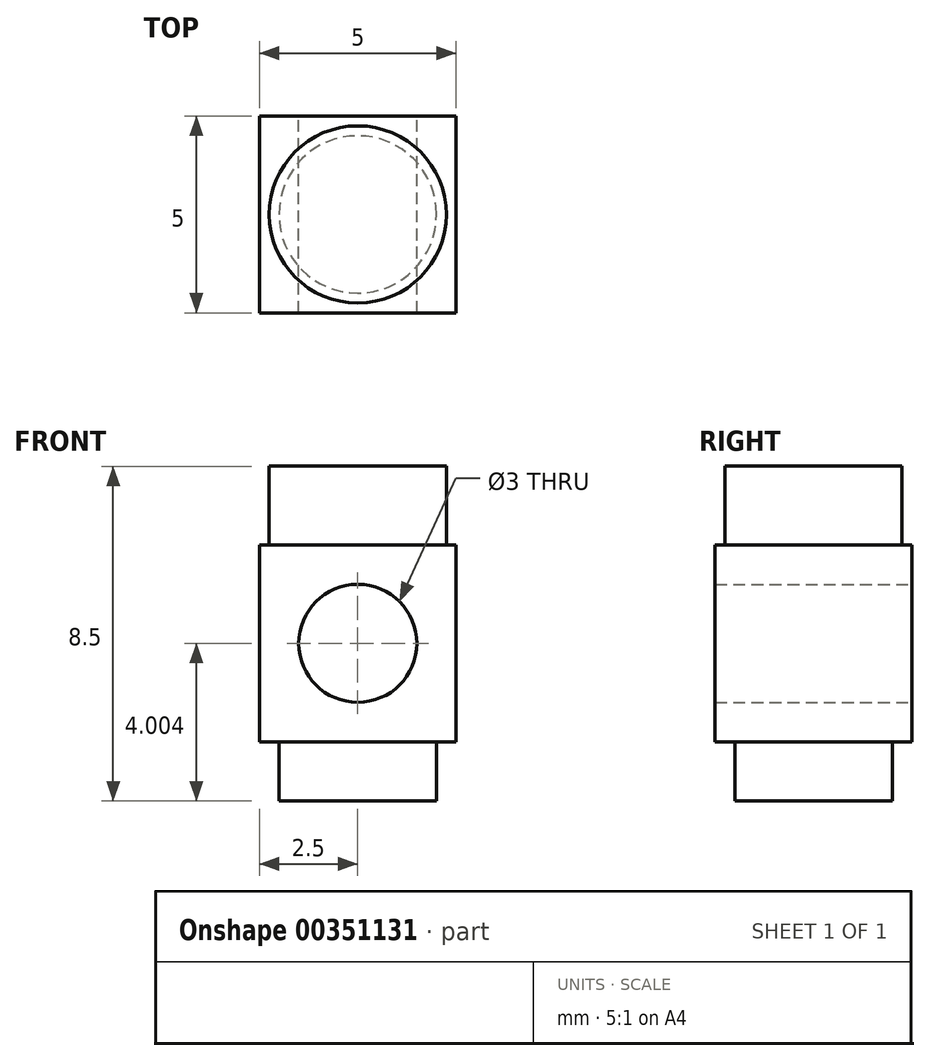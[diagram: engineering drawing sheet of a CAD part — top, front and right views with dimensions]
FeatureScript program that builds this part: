
annotation { "Feature Type Name" : "Feature", "Feature Type Description" : "" }
export const myFeature = defineFeature(function(context is Context, id is Id, definition is map)
    precondition{}
    {
        {
            var Q0;
            Q0=qCreatedBy(makeId("Front.planeOp"),FACE);
            var sketch = newSketch(context, id + "F0", { "sketchPlane" : qUnion([Q0])});
            skLineSegment(sketch, "E0.bottom", {"start": v(0, 12.57) * mm, "end": v(5, 12.57) * mm});
            skLineSegment(sketch, "E0.top", {"start": v(0, 17.57) * mm, "end": v(5, 17.57) * mm});
            skLineSegment(sketch, "E0.left", {"start": v(0, 12.57) * mm, "end": v(0, 17.57) * mm});
            skLineSegment(sketch, "E0.right", {"start": v(5, 12.57) * mm, "end": v(5, 17.57) * mm});
            skLineSegment(sketch, "E1", {"start": v(0, 17.57) * mm, "end": v(2.5, 17.57) * mm, "construction": true});
            skLineSegment(sketch, "E2", {"start": v(2.5, 17.57) * mm, "end": v(2.5, 12.57) * mm, "construction": true});
            skLineSegment(sketch, "E3", {"start": v(2.5, 12.57) * mm, "end": v(0, 12.57) * mm, "construction": true});
            skLineSegment(sketch, "E4", {"start": v(0, 15.07) * mm, "end": v(5, 15.07) * mm, "construction": true});
            skPoint(sketch, "E5", {"position": v(2.5, 15.07) * mm});
            skSolve(sketch);
        }
        {
            var Q0;
            Q0=makeQuery(id+"F0.imprint","IMPRINT",FACE,{"disambiguationData":[TD([[makeQuery(id+"F0.imprint","IMPRINT",EDGE,{"derivedFrom":sQuery(id+"F0.wireOp",EDGE,"E0.bottom")}),1.0]])]});
            extrude(context, id + "F1", {"entities" : qUnion([Q0]), "depth" : 5 * mm});
        }
        {
            var Q0;
            Q0=sQuery(id+"F0.wireOp",VERTEX,"E5");
            var Q1;
            Q1=makeQuery(id+"F1.opExtrude","SWEPT_BODY",BODY,{"disambiguationData":[OSD([sQuery(id+"F0.wireOp",EDGE,"E0.bottom"),sQuery(id+"F0.wireOp",EDGE,"E0.top"),sQuery(id+"F0.wireOp",EDGE,"E0.left"),sQuery(id+"F0.wireOp",EDGE,"E0.right")])]});
            hole(context, id + "F2", {"style" : HoleStyle.SIMPLE, "endStyle" : HoleEndStyle.THROUGH, "oppositeDirection" : true, "holeDiameter" : 3 * mm, "isTappedThrough" : true, "tappedDepth" : 12 * mm, "tapClearance" : 3, "locations" : qUnion([Q0]), "scope" : qUnion([Q1])});
        }
        {
            var Q0;
            Q0=makeQuery(id+"F1.opExtrude","SWEPT_FACE",FACE,{"disambiguationData":[OSD([sQuery(id+"F0.wireOp",EDGE,"E0.top")])]});
            var sketch = newSketch(context, id + "F3", { "sketchPlane" : qUnion([Q0])});
            skLineSegment(sketch, "E6", {"start": v(2.5, 0) * mm, "end": v(2.5, -5) * mm, "construction": true});
            skLineSegment(sketch, "E7", {"start": v(2.5, -5) * mm, "end": v(5, -5) * mm, "construction": true});
            skLineSegment(sketch, "E8", {"start": v(5, -5) * mm, "end": v(5, -2.5) * mm, "construction": true});
            skLineSegment(sketch, "E9", {"start": v(5, -2.5) * mm, "end": v(0, -2.5) * mm, "construction": true});
            skCircle(sketch, "E10", {"center": v(2.5, -2.5) * mm, "radius": 2.25 * mm});
            skSolve(sketch);
        }
        {
            var Q0;
            Q0 = qSketchRegion(id + "F3", true);
            extrude(context, id + "F4", {"entities" : qUnion([Q0]), "operationType" : NewBodyOperationType.ADD, "depth" : 2 * mm});
        }
        {
            var Q0;
            Q0=makeQuery(id+"F1.opExtrude","SWEPT_FACE",FACE,{"disambiguationData":[OSD([sQuery(id+"F0.wireOp",EDGE,"E0.bottom")])]});
            var sketch = newSketch(context, id + "F5", { "sketchPlane" : qUnion([Q0])});
            skLineSegment(sketch, "E11", {"start": v(2.5, 5) * mm, "end": v(2.5, 0) * mm});
            skLineSegment(sketch, "E12", {"start": v(0, 2.5) * mm, "end": v(5, 2.5) * mm});
            skPoint(sketch, "E13", {"position": v(2.5, 2.5) * mm});
            skCircle(sketch, "E14", {"center": v(2.5, 2.5) * mm, "radius": 2 * mm});
            skSolve(sketch);
        }
        {
            var Q0;
            {var subQ0=sQuery(id+"F5.wireOp",EDGE,"E14");var subQ1=sQuery(id+"F5.wireOp",EDGE,"E11");var subQ2=makeQuery(id+"F5.imprint","INTERSECT",VERTEX,{"disambiguationData":[OD(0.0)],"derivedFrom":[subQ1,subQ0]});Q0=makeQuery(id+"F5.imprint","IMPRINT",FACE,{"disambiguationData":[TD([[makeQuery(id+"F5.imprint","IMPRINT",EDGE,{"disambiguationData":[TD([[subQ2,-1.0]])],"derivedFrom":subQ1}),-1.0]])]});}
            var Q1;
            {var subQ0=sQuery(id+"F5.wireOp",EDGE,"E14");var subQ1=sQuery(id+"F5.wireOp",EDGE,"E11");var subQ2=makeQuery(id+"F5.imprint","INTERSECT",VERTEX,{"disambiguationData":[OD(0.0)],"derivedFrom":[subQ1,subQ0]});Q1=makeQuery(id+"F5.imprint","IMPRINT",FACE,{"disambiguationData":[TD([[makeQuery(id+"F5.imprint","IMPRINT",EDGE,{"disambiguationData":[TD([[subQ2,-1.0]])],"derivedFrom":subQ1}),1.0]])]});}
            var Q2;
            {var subQ0=sQuery(id+"F5.wireOp",EDGE,"E12");var subQ1=sQuery(id+"F5.wireOp",EDGE,"E11");var subQ2=makeQuery(id+"F5.imprint","INTERSECT",VERTEX,{"derivedFrom":[subQ1,subQ0]});Q2=makeQuery(id+"F5.imprint","IMPRINT",FACE,{"disambiguationData":[TD([[makeQuery(id+"F5.imprint","IMPRINT",EDGE,{"disambiguationData":[TD([[subQ2,-1.0]])],"derivedFrom":subQ1}),1.0]])]});}
            var Q3;
            {var subQ0=sQuery(id+"F5.wireOp",EDGE,"E12");var subQ1=sQuery(id+"F5.wireOp",EDGE,"E11");var subQ2=makeQuery(id+"F5.imprint","INTERSECT",VERTEX,{"derivedFrom":[subQ1,subQ0]});Q3=makeQuery(id+"F5.imprint","IMPRINT",FACE,{"disambiguationData":[TD([[makeQuery(id+"F5.imprint","IMPRINT",EDGE,{"disambiguationData":[TD([[subQ2,-1.0]])],"derivedFrom":subQ1}),-1.0]])]});}
            extrude(context, id + "F6", {"entities" : qUnion([Q0, Q1, Q2, Q3]), "operationType" : NewBodyOperationType.ADD, "depth" : 1.5 * mm});
        }
    });
